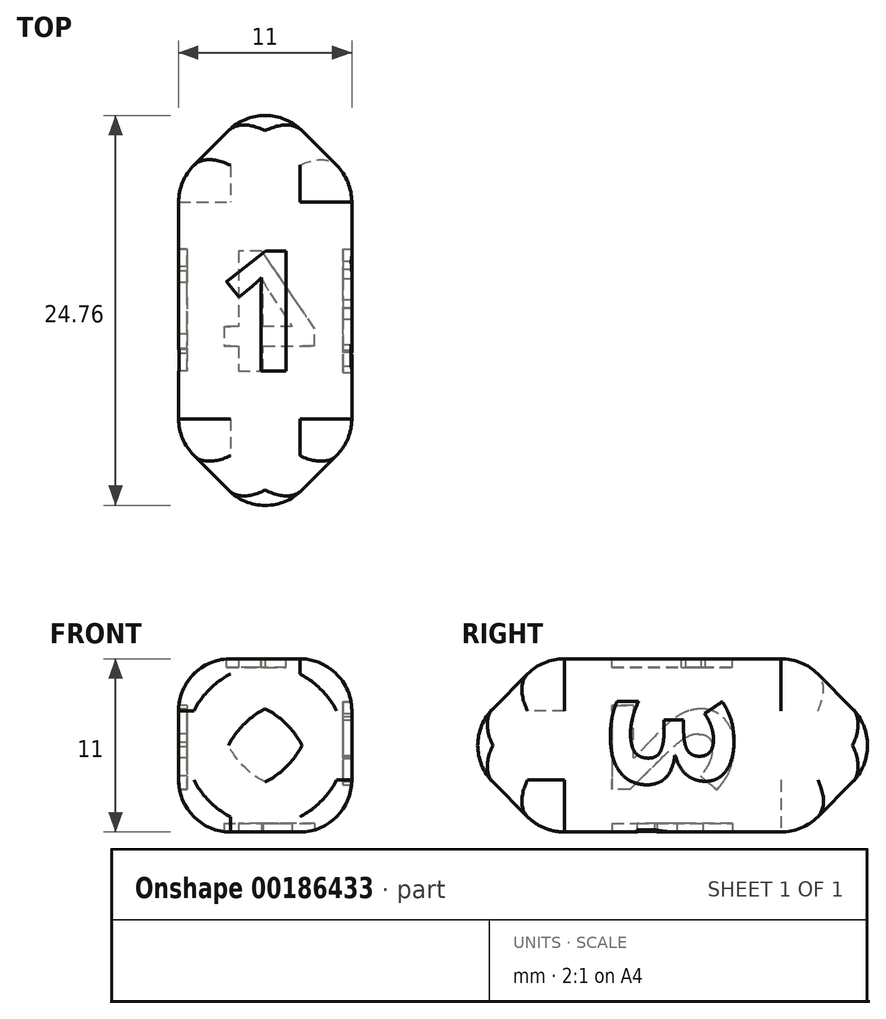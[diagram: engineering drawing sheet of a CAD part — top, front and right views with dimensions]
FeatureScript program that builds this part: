
annotation { "Feature Type Name" : "Feature", "Feature Type Description" : "" }
export const myFeature = defineFeature(function(context is Context, id is Id, definition is map)
    precondition{}
    {
        {
            var Q0;
            Q0=qCreatedBy(makeId("Right.planeOp"),FACE);
            var sketch = newSketch(context, id + "F0", { "sketchPlane" : qUnion([Q0])});
            skLineSegment(sketch, "E0.bottom", {"start": v(5, 5) * mm, "end": v(-5, 5) * mm});
            skLineSegment(sketch, "E0.top", {"start": v(5, -5) * mm, "end": v(-5, -5) * mm});
            skLineSegment(sketch, "E0.left", {"start": v(5, 5) * mm, "end": v(5, -5) * mm});
            skLineSegment(sketch, "E0.right", {"start": v(-5, 5) * mm, "end": v(-5, -5) * mm});
            skPoint(sketch, "E0.middle", {"position": v(0, 0) * mm});
            skSolve(sketch);
        }
        {
            var Q0;
            Q0 = qSketchRegion(id + "F0", true);
            extrude(context, id + "F1", {"entities" : qUnion([Q0]), "depth" : 25 * mm});
        }
        {
            var Q0;
            Q0=makeQuery(id+"F1.opExtrude","CAP_EDGE",EDGE,{"disambiguationData":[OSD([sQuery(id+"F0.wireOp",EDGE,"E0.bottom")])],"isStart":false});
            var Q1;
            Q1=makeQuery(id+"F1.opExtrude","CAP_EDGE",EDGE,{"disambiguationData":[OSD([sQuery(id+"F0.wireOp",EDGE,"E0.right")])],"isStart":false});
            var Q2;
            Q2=makeQuery(id+"F1.opExtrude","CAP_EDGE",EDGE,{"disambiguationData":[OSD([sQuery(id+"F0.wireOp",EDGE,"E0.top")])],"isStart":false});
            var Q3;
            Q3=makeQuery(id+"F1.opExtrude","CAP_EDGE",EDGE,{"disambiguationData":[OSD([sQuery(id+"F0.wireOp",EDGE,"E0.left")])],"isStart":false});
            var Q4;
            Q4=makeQuery(id+"F1.opExtrude","CAP_EDGE",EDGE,{"disambiguationData":[OSD([sQuery(id+"F0.wireOp",EDGE,"E0.left")])],"isStart":true});
            var Q5;
            Q5=makeQuery(id+"F1.opExtrude","CAP_EDGE",EDGE,{"disambiguationData":[OSD([sQuery(id+"F0.wireOp",EDGE,"E0.top")])],"isStart":true});
            var Q6;
            Q6=makeQuery(id+"F1.opExtrude","CAP_EDGE",EDGE,{"disambiguationData":[OSD([sQuery(id+"F0.wireOp",EDGE,"E0.right")])],"isStart":true});
            var Q7;
            Q7=makeQuery(id+"F1.opExtrude","CAP_EDGE",EDGE,{"disambiguationData":[OSD([sQuery(id+"F0.wireOp",EDGE,"E0.bottom")])],"isStart":true});
            chamfer(context, id + "F2", {"entities" : qUnion([Q0, Q1, Q2, Q3, Q4, Q5, Q6, Q7]), "width" : 5 * mm, "tangentPropagation" : true});
        }
        {
            var Q0;
            Q0=makeQuery(id+"F1.opExtrude","SWEPT_EDGE",EDGE,{"disambiguationData":[OSD([sQuery(id+"F0.wireOp",EDGE,"E0.bottom"),sQuery(id+"F0.wireOp",EDGE,"E0.right")])]});
            var Q1;
            Q1=makeQuery(id+"F1.opExtrude","SWEPT_EDGE",EDGE,{"disambiguationData":[OSD([sQuery(id+"F0.wireOp",EDGE,"E0.top"),sQuery(id+"F0.wireOp",EDGE,"E0.right")])]});
            var Q2;
            Q2=makeQuery(id+"F2.opChamfer","BLEND_EDGE",EDGE,{"blendedFrom":[makeQuery(id+"F1.opExtrude","CAP_EDGE",EDGE,{"disambiguationData":[OSD([sQuery(id+"F0.wireOp",EDGE,"E0.top")])],"isStart":false}),makeQuery(id+"F1.opExtrude","CAP_EDGE",EDGE,{"disambiguationData":[OSD([sQuery(id+"F0.wireOp",EDGE,"E0.right")])],"isStart":false})],"blendedInto":[]});
            var Q3;
            Q3=makeQuery(id+"F2.opChamfer","BLEND_EDGE",EDGE,{"blendedFrom":[makeQuery(id+"F1.opExtrude","CAP_EDGE",EDGE,{"disambiguationData":[OSD([sQuery(id+"F0.wireOp",EDGE,"E0.bottom")])],"isStart":false}),makeQuery(id+"F1.opExtrude","CAP_EDGE",EDGE,{"disambiguationData":[OSD([sQuery(id+"F0.wireOp",EDGE,"E0.left")])],"isStart":false})],"blendedInto":[]});
            var Q4;
            Q4=makeQuery(id+"F1.opExtrude","SWEPT_EDGE",EDGE,{"disambiguationData":[OSD([sQuery(id+"F0.wireOp",EDGE,"E0.bottom"),sQuery(id+"F0.wireOp",EDGE,"E0.left")])]});
            var Q5;
            Q5=makeQuery(id+"F1.opExtrude","SWEPT_EDGE",EDGE,{"disambiguationData":[OSD([sQuery(id+"F0.wireOp",EDGE,"E0.top"),sQuery(id+"F0.wireOp",EDGE,"E0.left")])]});
            var Q6;
            {var subQ0=sQuery(id+"F0.wireOp",EDGE,"E0.left");Q6=makeQuery(id+"F2.opChamfer","BLEND_EDGE",EDGE,{"blendedFrom":[makeQuery(id+"F1.opExtrude","CAP_EDGE",EDGE,{"disambiguationData":[OSD([subQ0])],"isStart":true}),makeQuery(id+"F1.opExtrude","SWEPT_FACE",FACE,{"disambiguationData":[OSD([subQ0])]})],"blendedInto":[makeQuery(id+"F1.opExtrude","SWEPT_FACE",FACE,{"disambiguationData":[OSD([subQ0])]})]});}
            var Q7;
            {var subQ0=sQuery(id+"F0.wireOp",EDGE,"E0.top");Q7=makeQuery(id+"F2.opChamfer","BLEND_EDGE",EDGE,{"blendedFrom":[makeQuery(id+"F1.opExtrude","CAP_EDGE",EDGE,{"disambiguationData":[OSD([subQ0])],"isStart":true}),makeQuery(id+"F1.opExtrude","SWEPT_FACE",FACE,{"disambiguationData":[OSD([subQ0])]})],"blendedInto":[makeQuery(id+"F1.opExtrude","SWEPT_FACE",FACE,{"disambiguationData":[OSD([subQ0])]})]});}
            var Q8;
            {var subQ0=sQuery(id+"F0.wireOp",EDGE,"E0.right");Q8=makeQuery(id+"F2.opChamfer","BLEND_EDGE",EDGE,{"blendedFrom":[makeQuery(id+"F1.opExtrude","CAP_EDGE",EDGE,{"disambiguationData":[OSD([subQ0])],"isStart":true}),makeQuery(id+"F1.opExtrude","SWEPT_FACE",FACE,{"disambiguationData":[OSD([subQ0])]})],"blendedInto":[makeQuery(id+"F1.opExtrude","SWEPT_FACE",FACE,{"disambiguationData":[OSD([subQ0])]})]});}
            var Q9;
            Q9=makeQuery(id+"F2.opChamfer","BLEND_EDGE",EDGE,{"blendedFrom":[makeQuery(id+"F1.opExtrude","CAP_EDGE",EDGE,{"disambiguationData":[OSD([sQuery(id+"F0.wireOp",EDGE,"E0.top")])],"isStart":true}),makeQuery(id+"F1.opExtrude","CAP_EDGE",EDGE,{"disambiguationData":[OSD([sQuery(id+"F0.wireOp",EDGE,"E0.right")])],"isStart":true})],"blendedInto":[]});
            var Q10;
            Q10=makeQuery(id+"F2.opChamfer","BLEND_EDGE",EDGE,{"blendedFrom":[makeQuery(id+"F1.opExtrude","CAP_EDGE",EDGE,{"disambiguationData":[OSD([sQuery(id+"F0.wireOp",EDGE,"E0.top")])],"isStart":true}),makeQuery(id+"F1.opExtrude","CAP_EDGE",EDGE,{"disambiguationData":[OSD([sQuery(id+"F0.wireOp",EDGE,"E0.left")])],"isStart":true})],"blendedInto":[]});
            var Q11;
            {var subQ0=sQuery(id+"F0.wireOp",EDGE,"E0.bottom");Q11=makeQuery(id+"F2.opChamfer","BLEND_EDGE",EDGE,{"blendedFrom":[makeQuery(id+"F1.opExtrude","CAP_EDGE",EDGE,{"disambiguationData":[OSD([subQ0])],"isStart":true}),makeQuery(id+"F1.opExtrude","SWEPT_FACE",FACE,{"disambiguationData":[OSD([subQ0])]})],"blendedInto":[makeQuery(id+"F1.opExtrude","SWEPT_FACE",FACE,{"disambiguationData":[OSD([subQ0])]})]});}
            var Q12;
            Q12=makeQuery(id+"F2.opChamfer","BLEND_EDGE",EDGE,{"blendedFrom":[makeQuery(id+"F1.opExtrude","CAP_EDGE",EDGE,{"disambiguationData":[OSD([sQuery(id+"F0.wireOp",EDGE,"E0.bottom")])],"isStart":true}),makeQuery(id+"F1.opExtrude","CAP_EDGE",EDGE,{"disambiguationData":[OSD([sQuery(id+"F0.wireOp",EDGE,"E0.right")])],"isStart":true})],"blendedInto":[]});
            var Q13;
            Q13=makeQuery(id+"F2.opChamfer","BLEND_EDGE",EDGE,{"blendedFrom":[makeQuery(id+"F1.opExtrude","CAP_EDGE",EDGE,{"disambiguationData":[OSD([sQuery(id+"F0.wireOp",EDGE,"E0.bottom")])],"isStart":true}),makeQuery(id+"F1.opExtrude","CAP_EDGE",EDGE,{"disambiguationData":[OSD([sQuery(id+"F0.wireOp",EDGE,"E0.left")])],"isStart":true})],"blendedInto":[]});
            fillet(context, id + "F3", {"entities" : qUnion([Q0, Q1, Q2, Q3, Q4, Q5, Q6, Q7, Q8, Q9, Q10, Q11, Q12, Q13]), "radius" : 3 * mm, "tangentPropagation" : true, "allowEdgeOverflow" : false});
        }
        {
            var Q0;
            Q0=makeQuery(id+"F2.opChamfer","BLEND_EDGE",EDGE,{"blendedFrom":[makeQuery(id+"F1.opExtrude","CAP_EDGE",EDGE,{"disambiguationData":[OSD([sQuery(id+"F0.wireOp",EDGE,"E0.top")])],"isStart":false}),makeQuery(id+"F1.opExtrude","CAP_EDGE",EDGE,{"disambiguationData":[OSD([sQuery(id+"F0.wireOp",EDGE,"E0.left")])],"isStart":false})],"blendedInto":[]});
            var Q1;
            {var subQ0=sQuery(id+"F0.wireOp",EDGE,"E0.top");Q1=makeQuery(id+"F2.opChamfer","BLEND_EDGE",EDGE,{"blendedFrom":[makeQuery(id+"F1.opExtrude","CAP_EDGE",EDGE,{"disambiguationData":[OSD([subQ0])],"isStart":false}),makeQuery(id+"F1.opExtrude","SWEPT_FACE",FACE,{"disambiguationData":[OSD([subQ0])]})],"blendedInto":[makeQuery(id+"F1.opExtrude","SWEPT_FACE",FACE,{"disambiguationData":[OSD([subQ0])]})]});}
            var Q2;
            {var subQ0=sQuery(id+"F0.wireOp",EDGE,"E0.left");Q2=makeQuery(id+"F2.opChamfer","BLEND_EDGE",EDGE,{"blendedFrom":[makeQuery(id+"F1.opExtrude","CAP_EDGE",EDGE,{"disambiguationData":[OSD([subQ0])],"isStart":false}),makeQuery(id+"F1.opExtrude","SWEPT_FACE",FACE,{"disambiguationData":[OSD([subQ0])]})],"blendedInto":[makeQuery(id+"F1.opExtrude","SWEPT_FACE",FACE,{"disambiguationData":[OSD([subQ0])]})]});}
            fillet(context, id + "F4", {"entities" : qUnion([Q0, Q1, Q2]), "radius" : 3 * mm, "tangentPropagation" : true, "allowEdgeOverflow" : false});
        }
        {
            var Q0;
            Q0=qCreatedBy(makeId("Front.planeOp"),FACE);
            var sketch = newSketch(context, id + "F5", { "sketchPlane" : qUnion([Q0])});
            skLineSegment(sketch, "E1", {"start": v(0, 0) * mm, "end": v(0, 30) * mm, "construction": true});
            skSolve(sketch);
        }
        {
            var Q0;
            Q0=makeQuery(id+"F1.opExtrude","SWEPT_BODY",BODY,{"disambiguationData":[OSD([sQuery(id+"F0.wireOp",EDGE,"E0.bottom"),sQuery(id+"F0.wireOp",EDGE,"E0.top"),sQuery(id+"F0.wireOp",EDGE,"E0.left"),sQuery(id+"F0.wireOp",EDGE,"E0.right")])]});
            var Q1;
            Q1=sQuery(id+"F5.wireOp",EDGE,"E1");
            transform(context, id + "F6", {"entities" : qUnion([Q0]), "transformType" : TransformType.ROTATION, "transformAxis" : qUnion([Q1]), "angle" : 90 * degree, "makeCopy" : false});
        }
        {
            var Q0;
            Q0=makeQuery(id+"F1.opExtrude","SWEPT_FACE",FACE,{"disambiguationData":[OSD([sQuery(id+"F0.wireOp",EDGE,"E0.top")])]});
            var sketch = newSketch(context, id + "F7", { "sketchPlane" : qUnion([Q0])});
            skPoint(sketch, "E2", {"position": v(2, -12.5) * mm});
            skText(sketch, "E3", { "text": "4", "fontName": "OpenSans-Bold.ttf"});
            const initialGuessF7  = {"E3": [0.00301, -0.009, -1, 0, 0.007]};
            skSetInitialGuess(sketch, initialGuessF7);
            skSolve(sketch);
        }
        {
            var Q0;
            Q0=makeQuery(id+"F1.opExtrude","SWEPT_FACE",FACE,{"disambiguationData":[OSD([sQuery(id+"F0.wireOp",EDGE,"E0.bottom")])]});
            var sketch = newSketch(context, id + "F8", { "sketchPlane" : qUnion([Q0])});
            skPoint(sketch, "E4", {"position": v(-2, 12.5) * mm});
            skText(sketch, "E5", { "text": "1", "fontName": "OpenSans-Bold.ttf"});
            const initialGuessF8  = {"E5": [-0.0028, 0.009, 1, 0, 0.007]};
            skSetInitialGuess(sketch, initialGuessF8);
            skSolve(sketch);
        }
        {
            var Q0;
            Q0=makeQuery(id+"F1.opExtrude","SWEPT_FACE",FACE,{"disambiguationData":[OSD([sQuery(id+"F0.wireOp",EDGE,"E0.right")])]});
            var sketch = newSketch(context, id + "F9", { "sketchPlane" : qUnion([Q0])});
            skText(sketch, "E6", { "text": "3", "fontName": "OpenSans-Bold.ttf"});
            const initialGuessF9  = {"E6": [0.009, 0.0029, 0, -1, 0.007]};
            skSetInitialGuess(sketch, initialGuessF9);
            skSolve(sketch);
        }
        {
            var Q0;
            Q0=makeQuery(id+"F1.opExtrude","SWEPT_FACE",FACE,{"disambiguationData":[OSD([sQuery(id+"F0.wireOp",EDGE,"E0.left")])]});
            var sketch = newSketch(context, id + "F10", { "sketchPlane" : qUnion([Q0])});
            skText(sketch, "E7", { "text": "2", "fontName": "OpenSans-Bold.ttf"});
            const initialGuessF10  = {"E7": [-0.009, -0.00294, 0, 1, 0.007]};
            skSetInitialGuess(sketch, initialGuessF10);
            skSolve(sketch);
        }
        {
            var Q0;
            Q0 = qSketchRegion(id + "F8", true);
            extrude(context, id + "F11", {"entities" : qUnion([Q0]), "operationType" : NewBodyOperationType.REMOVE, "oppositeDirection" : true, "depth" : 0.5 * mm});
        }
        {
            var Q0;
            Q0 = qSketchRegion(id + "F10", true);
            extrude(context, id + "F12", {"entities" : qUnion([Q0]), "operationType" : NewBodyOperationType.REMOVE, "oppositeDirection" : true, "depth" : 0.5 * mm});
        }
        {
            var Q0;
            Q0 = qSketchRegion(id + "F9", true);
            extrude(context, id + "F13", {"entities" : qUnion([Q0]), "operationType" : NewBodyOperationType.REMOVE, "oppositeDirection" : true, "depth" : 0.5 * mm});
        }
        {
            var Q0;
            Q0 = qSketchRegion(id + "F7", true);
            extrude(context, id + "F14", {"entities" : qUnion([Q0]), "operationType" : NewBodyOperationType.REMOVE, "oppositeDirection" : true, "depth" : 0.5 * mm});
        }
        {
            var Q0;
            Q0=makeQuery(id+"F1.opExtrude","SWEPT_BODY",BODY,{"disambiguationData":[OSD([sQuery(id+"F0.wireOp",EDGE,"E0.bottom"),sQuery(id+"F0.wireOp",EDGE,"E0.top"),sQuery(id+"F0.wireOp",EDGE,"E0.left"),sQuery(id+"F0.wireOp",EDGE,"E0.right")])]});
            var Q1;
            Q1=qCreatedBy(makeId("Origin.pointOp"),VERTEX);
            transform(context, id + "F15", {"entities" : qUnion([Q0]), "transformType" : TransformType.SCALE_UNIFORMLY, "scale" : 1.1, "scalePoint" : qUnion([Q1]), "makeCopy" : false});
        }
    });
